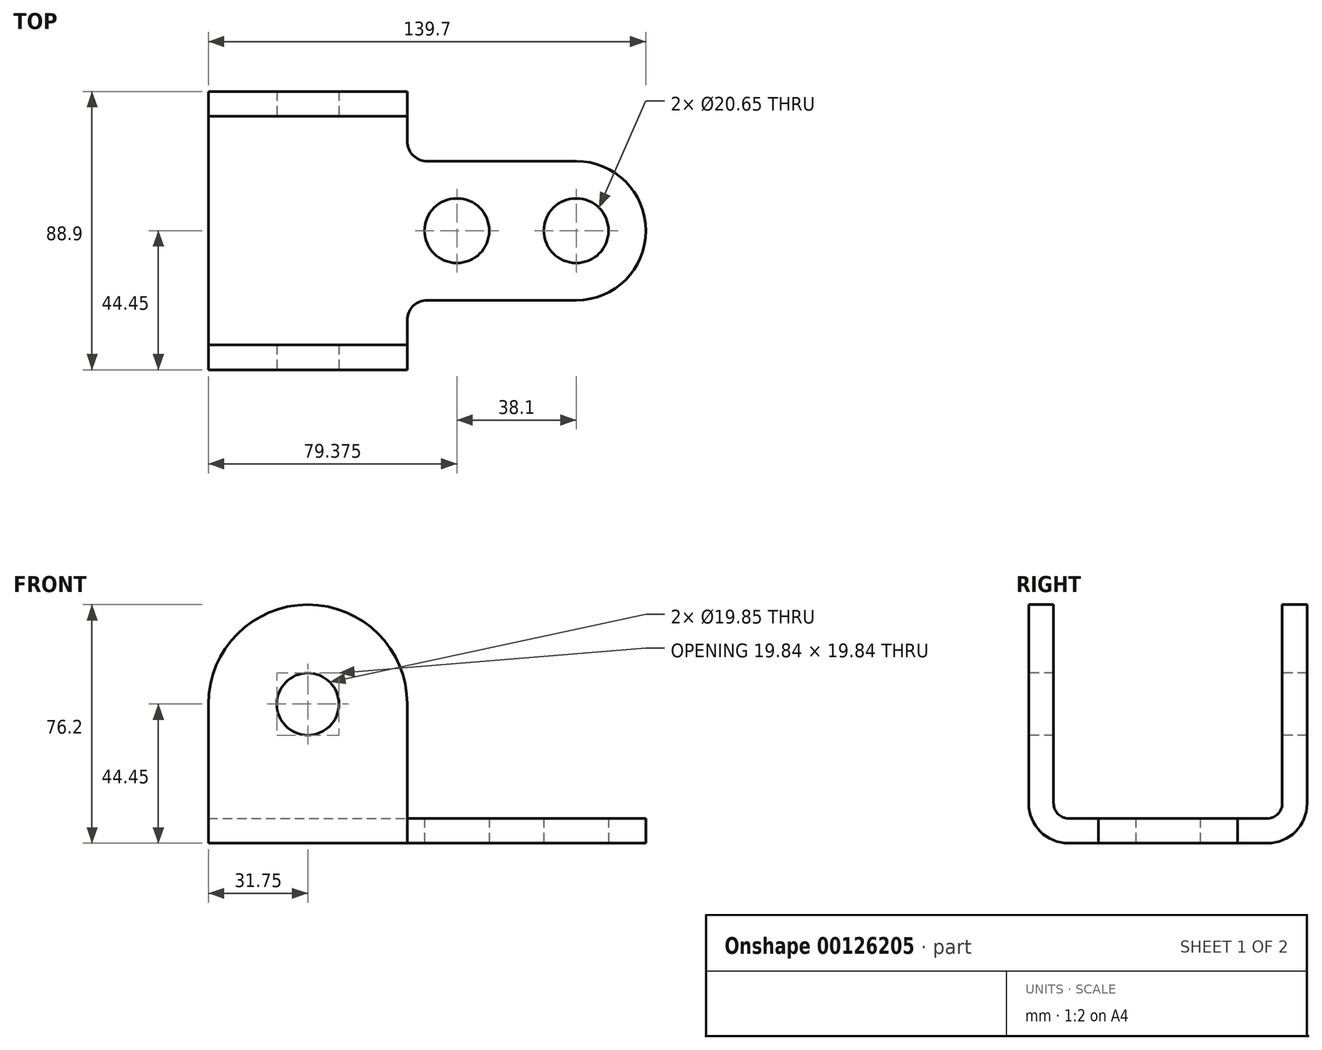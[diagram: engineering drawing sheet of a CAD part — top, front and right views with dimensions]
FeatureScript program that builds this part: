
annotation { "Feature Type Name" : "Feature", "Feature Type Description" : "" }
export const myFeature = defineFeature(function(context is Context, id is Id, definition is map)
    precondition{}
    {
        {
            var Q0;
            Q0=qCreatedBy(makeId("Top.planeOp"),FACE);
            var sketch = newSketch(context, id + "F0", { "sketchPlane" : qUnion([Q0])});
            skLineSegment(sketch, "E0", {"start": v(0, 0) * mm, "end": v(0, 88.9) * mm});
            skLineSegment(sketch, "E1", {"start": v(0, 88.9) * mm, "end": v(63.5, 88.9) * mm});
            skLineSegment(sketch, "E2", {"start": v(63.5, 88.9) * mm, "end": v(63.5, 73.03) * mm});
            skLineSegment(sketch, "E3", {"start": v(69.85, 66.68) * mm, "end": v(117.48, 66.68) * mm});
            skArc(sketch, "E4", {"start": v(117.48, 22.23) * mm, "mid": v(139.7, 44.45) * mm, "end": v(117.48, 66.68) * mm});
            skLineSegment(sketch, "E5", {"start": v(117.48, 22.23) * mm, "end": v(69.85, 22.23) * mm});
            skLineSegment(sketch, "E6", {"start": v(63.5, 15.88) * mm, "end": v(63.5, 0) * mm});
            skLineSegment(sketch, "E7", {"start": v(63.5, 0) * mm, "end": v(0, 0) * mm});
            skCircle(sketch, "E8", {"center": v(117.48, 44.45) * mm, "radius": 10.33 * mm});
            skCircle(sketch, "E9", {"center": v(79.38, 44.45) * mm, "radius": 10.33 * mm});
            skPoint(sketch, "E10.visualSharp", {"position": v(63.5, 66.68) * mm});
            skArc(sketch, "E10.filletArc", {"start": v(63.5, 73.03) * mm, "mid": v(65.36, 68.53) * mm, "end": v(69.85, 66.67) * mm});
            skPoint(sketch, "E11.visualSharp", {"position": v(63.5, 22.22) * mm});
            skArc(sketch, "E11.filletArc", {"start": v(69.85, 22.23) * mm, "mid": v(65.36, 20.37) * mm, "end": v(63.5, 15.88) * mm});
            skSolve(sketch);
        }
        {
            var Q0;
            Q0=qCreatedBy(makeId("Front.planeOp"),FACE);
            var sketch = newSketch(context, id + "F1", { "sketchPlane" : qUnion([Q0])});
            skLineSegment(sketch, "E12", {"start": v(0, 0) * mm, "end": v(0, 44.45) * mm});
            skArc(sketch, "E13", {"start": v(63.5, 44.45) * mm, "mid": v(31.75, 76.2) * mm, "end": v(0, 44.45) * mm});
            skLineSegment(sketch, "E14", {"start": v(63.5, 44.45) * mm, "end": v(63.5, 0) * mm});
            skLineSegment(sketch, "E15", {"start": v(0, 0) * mm, "end": v(63.5, 0) * mm});
            skCircle(sketch, "E16", {"center": v(31.75, 44.45) * mm, "radius": 9.92 * mm});
            skSolve(sketch);
        }
        {
            var Q0;
            Q0=makeQuery(id+"F0.imprint","IMPRINT",FACE,{"disambiguationData":[TD([[makeQuery(id+"F0.imprint","IMPRINT",EDGE,{"derivedFrom":sQuery(id+"F0.wireOp",EDGE,"E0")}),-1.0]])]});
            extrude(context, id + "F2", {"entities" : qUnion([Q0]), "depth" : 7.94 * mm});
        }
        {
            var Q0;
            Q0=makeQuery(id+"F1.imprint","IMPRINT",FACE,{"disambiguationData":[TD([[makeQuery(id+"F1.imprint","IMPRINT",EDGE,{"derivedFrom":sQuery(id+"F1.wireOp",EDGE,"E12")}),-1.0]])]});
            extrude(context, id + "F3", {"entities" : qUnion([Q0]), "operationType" : NewBodyOperationType.ADD, "oppositeDirection" : true, "depth" : 88.9 * mm});
        }
        {
            var Q0;
            Q0=makeQuery(id+"F3.boolean.opBoolean","MERGE",FACE,{"derivedFrom":[makeQuery(id+"F2.opExtrude","SWEPT_FACE",FACE,{"disambiguationData":[OSD([sQuery(id+"F0.wireOp",EDGE,"E2")])]}),makeQuery(id+"F2.opExtrude","SWEPT_FACE",FACE,{"disambiguationData":[OSD([sQuery(id+"F0.wireOp",EDGE,"E6")])]}),makeQuery(id+"F3.opExtrude","SWEPT_FACE",FACE,{"disambiguationData":[OSD([sQuery(id+"F1.wireOp",EDGE,"E14")])]})]});
            var sketch = newSketch(context, id + "F4", { "sketchPlane" : qUnion([Q0])});
            skLineSegment(sketch, "E17.bottom", {"start": v(80.96, 7.94) * mm, "end": v(7.94, 7.94) * mm});
            skLineSegment(sketch, "E17.top", {"start": v(80.96, 84.14) * mm, "end": v(7.94, 84.14) * mm});
            skLineSegment(sketch, "E17.left", {"start": v(80.96, 7.94) * mm, "end": v(80.96, 84.14) * mm});
            skLineSegment(sketch, "E17.right", {"start": v(7.94, 7.94) * mm, "end": v(7.94, 84.14) * mm});
            skSolve(sketch);
        }
        {
            var Q0;
            Q0 = qSketchRegion(id + "F4", true);
            extrude(context, id + "F5", {"entities" : qUnion([Q0]), "operationType" : NewBodyOperationType.REMOVE, "endBound" : BoundingType.THROUGH_ALL, "oppositeDirection" : true, "depth" : 25.4 * mm});
        }
        {
            var Q0;
            Q0=makeQuery(id+"F2.opExtrude","CAP_EDGE",EDGE,{"disambiguationData":[OSD([sQuery(id+"F0.wireOp",EDGE,"E7")])],"isStart":true});
            var Q1;
            Q1=makeQuery(id+"F2.opExtrude","CAP_EDGE",EDGE,{"disambiguationData":[OSD([sQuery(id+"F0.wireOp",EDGE,"E1")])],"isStart":true});
            fillet(context, id + "F6", {"entities" : qUnion([Q0, Q1]), "radius" : 12.7 * mm, "tangentPropagation" : true, "allowEdgeOverflow" : false});
        }
        {
            var Q0;
            Q0=makeQuery(id+"F5.boolean.opBoolean","COPY",EDGE,{"derivedFrom":makeQuery(id+"F5.opExtrude","SWEPT_EDGE",EDGE,{"disambiguationData":[OSD([sQuery(id+"F4.wireOp",EDGE,"E17.bottom"),sQuery(id+"F4.wireOp",EDGE,"E17.right")])]})});
            var Q1;
            Q1=makeQuery(id+"F5.boolean.opBoolean","COPY",EDGE,{"derivedFrom":makeQuery(id+"F5.opExtrude","SWEPT_EDGE",EDGE,{"disambiguationData":[OSD([sQuery(id+"F4.wireOp",EDGE,"E17.bottom"),sQuery(id+"F4.wireOp",EDGE,"E17.left")])]})});
            fillet(context, id + "F7", {"entities" : qUnion([Q0, Q1]), "radius" : 4.76 * mm, "tangentPropagation" : true, "allowEdgeOverflow" : false});
        }
    });
